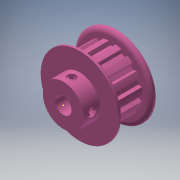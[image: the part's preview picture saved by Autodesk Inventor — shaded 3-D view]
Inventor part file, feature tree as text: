
AUTODESK INVENTOR PART (.ipt)
format: ipt  version: 2017 SP1 (Build 210196100, 196)  size: 266,752 bytes
history: native  units: in
note: dims shown in document units (in); Inventor stores cm internally (conversion verified against a paired STEP export)
features: extrude x3, sketch x3, projected_geometry x3, pattern_circular x1
ambient origin geometry x8: Origin, YZ Plane, XZ Plane, XY Plane, X Axis, Y Axis, Z Axis, Center Point
bodies: Solid1 (feature_tree)
feature tree (10):
  extrude  "Extrusion1"  Depth=1.0in TaperAngle=0.0deg
  extrude  "Extrusion2"  [1 undecoded]
  extrude  "Extrusion3"  [1 undecoded]
  sketch  "Sketch1"  dims[d0=1.0in d1=0.0in d2=0.0625in d3=0.0in]
  projected_geometry  "Projected Loop1"
  sketch  "Sketch2"  dims[d4=0.0625in d5=0.0in]
  projected_geometry  "Projected Loop2"
  sketch  "Sketch3"
  projected_geometry  "Projected Loop3"
  pattern_circular  "CirPattern2"
note: 2 required parameter values undecoded (feature->parameter linkage not recoverable at this tier; creation-order binding heuristic only, values carry confidence <= 0.55)
